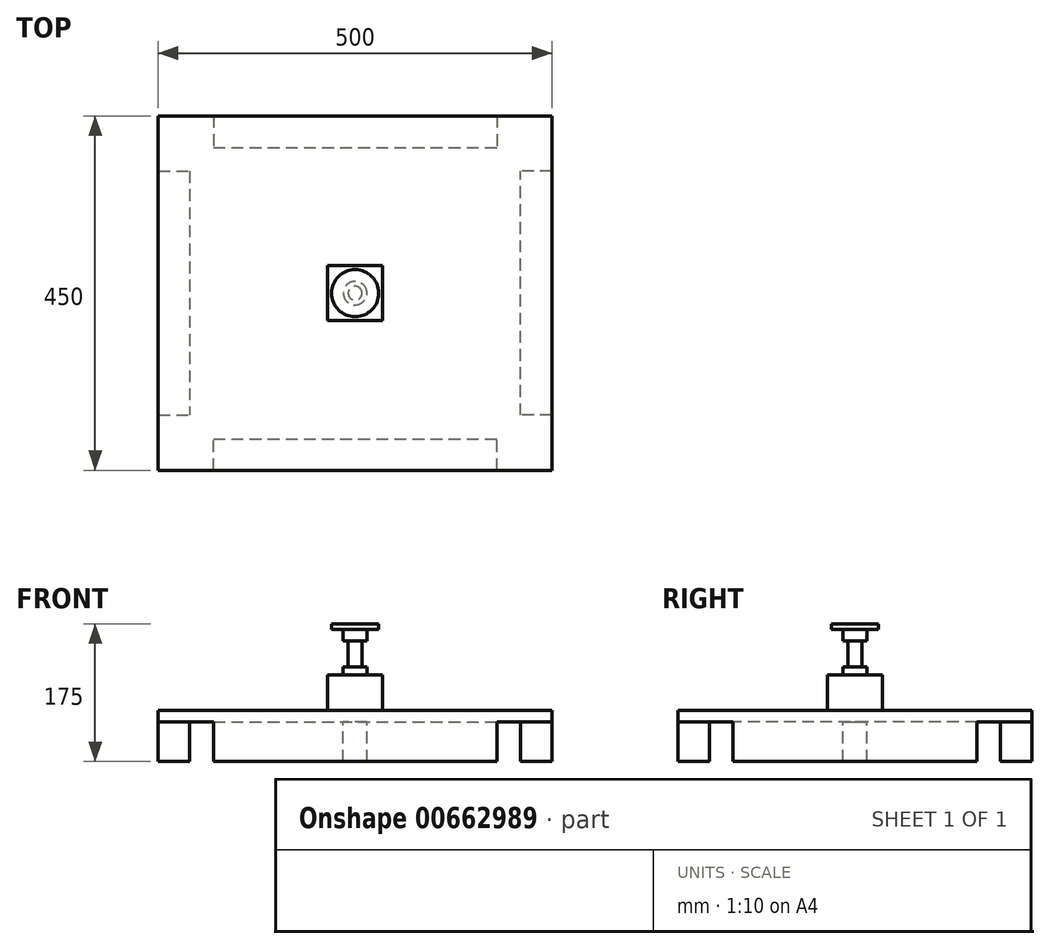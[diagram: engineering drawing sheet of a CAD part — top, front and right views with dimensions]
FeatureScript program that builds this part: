
annotation { "Feature Type Name" : "Feature", "Feature Type Description" : "" }
export const myFeature = defineFeature(function(context is Context, id is Id, definition is map)
    precondition{}
    {
        {
            var Q0;
            Q0=qCreatedBy(makeId("Top.planeOp"),FACE);
            var sketch = newSketch(context, id + "F0", { "sketchPlane" : qUnion([Q0])});
            skLineSegment(sketch, "E0.bottom", {"start": v(250, -225) * mm, "end": v(-250, -225) * mm});
            skLineSegment(sketch, "E0.top", {"start": v(250, 225) * mm, "end": v(-250, 225) * mm});
            skLineSegment(sketch, "E0.left", {"start": v(250, -225) * mm, "end": v(250, 225) * mm});
            skLineSegment(sketch, "E0.right", {"start": v(-250, -225) * mm, "end": v(-250, 225) * mm});
            skPoint(sketch, "E0.middle", {"position": v(0, 0) * mm});
            skLineSegment(sketch, "E1.bottom", {"start": v(-180, -225) * mm, "end": v(180, -225) * mm});
            skLineSegment(sketch, "E1.top", {"start": v(-180, -185) * mm, "end": v(180, -185) * mm});
            skLineSegment(sketch, "E1.left", {"start": v(-180, -225) * mm, "end": v(-180, -185) * mm});
            skLineSegment(sketch, "E1.right", {"start": v(180, -225) * mm, "end": v(180, -185) * mm});
            skLineSegment(sketch, "E2.bottom", {"start": v(250, -155) * mm, "end": v(210, -155) * mm});
            skLineSegment(sketch, "E2.top", {"start": v(250, 155) * mm, "end": v(210, 155) * mm});
            skLineSegment(sketch, "E2.left", {"start": v(250, -155) * mm, "end": v(250, 155) * mm});
            skLineSegment(sketch, "E2.right", {"start": v(210, -155) * mm, "end": v(210, 155) * mm});
            skLineSegment(sketch, "E3.bottom", {"start": v(-180, 225) * mm, "end": v(180, 225) * mm});
            skLineSegment(sketch, "E3.top", {"start": v(-180, 185) * mm, "end": v(180, 185) * mm});
            skLineSegment(sketch, "E3.left", {"start": v(-180, 225) * mm, "end": v(-180, 185) * mm});
            skLineSegment(sketch, "E3.right", {"start": v(180, 225) * mm, "end": v(180, 185) * mm});
            skLineSegment(sketch, "E4.bottom", {"start": v(-250, 155) * mm, "end": v(-210, 155) * mm});
            skLineSegment(sketch, "E4.top", {"start": v(-250, -155) * mm, "end": v(-210, -155) * mm});
            skLineSegment(sketch, "E4.left", {"start": v(-250, 155) * mm, "end": v(-250, -155) * mm});
            skLineSegment(sketch, "E4.right", {"start": v(-210, 155) * mm, "end": v(-210, -155) * mm});
            skLineSegment(sketch, "E5", {"start": v(180, 185) * mm, "end": v(210, 185) * mm, "construction": true});
            skLineSegment(sketch, "E6", {"start": v(210, 185) * mm, "end": v(210, 155) * mm, "construction": true});
            skLineSegment(sketch, "E7", {"start": v(210, -155) * mm, "end": v(210, -185) * mm, "construction": true});
            skLineSegment(sketch, "E8", {"start": v(210, -185) * mm, "end": v(180, -185) * mm, "construction": true});
            skLineSegment(sketch, "E9", {"start": v(-180, -185) * mm, "end": v(-210, -185) * mm, "construction": true});
            skLineSegment(sketch, "E10", {"start": v(-210, -185) * mm, "end": v(-210, -155) * mm, "construction": true});
            skLineSegment(sketch, "E11", {"start": v(-210, 155) * mm, "end": v(-210, 185) * mm, "construction": true});
            skLineSegment(sketch, "E12", {"start": v(-210, 185) * mm, "end": v(-180, 185) * mm, "construction": true});
            skSolve(sketch);
        }
        {
            var Q0;
            Q0=makeQuery(id+"F0.imprint","IMPRINT",FACE,{"disambiguationData":[TD([[makeQuery(id+"F0.imprint","IMPRINT",EDGE,{"derivedFrom":sQuery(id+"F0.wireOp",EDGE,"E1.top")}),1.0]])]});
            var Q1;
            {var subQ2=sQuery(id+"F0.wireOp",EDGE,"E4.bottom");Q1=makeQuery(id+"F0.imprint","IMPRINT",FACE,{"disambiguationData":[TD([[makeQuery(id+"F0.imprint","IMPRINT",EDGE,{"derivedFrom":subQ2}),-1.0]])]});}
            var Q2;
            Q2=makeQuery(id+"F0.imprint","IMPRINT",FACE,{"disambiguationData":[TD([[makeQuery(id+"F0.imprint","IMPRINT",EDGE,{"derivedFrom":sQuery(id+"F0.wireOp",EDGE,"E3.top")}),1.0]])]});
            var Q3;
            {var subQ0=sQuery(id+"F0.wireOp",EDGE,"E2.bottom");Q3=makeQuery(id+"F0.imprint","IMPRINT",FACE,{"disambiguationData":[TD([[makeQuery(id+"F0.imprint","IMPRINT",EDGE,{"derivedFrom":subQ0}),-1.0]])]});}
            var Q4;
            Q4=makeQuery(id+"F0.imprint","IMPRINT",FACE,{"disambiguationData":[TD([[makeQuery(id+"F0.imprint","IMPRINT",EDGE,{"derivedFrom":sQuery(id+"F0.wireOp",EDGE,"E1.top")}),-1.0]])]});
            extrude(context, id + "F1", {"entities" : qUnion([Q0, Q1, Q2, Q3, Q4]), "depth" : 15 * mm, "offsetDistance" : 25 * mm});
        }
        {
            var Q0;
            Q0=makeQuery(id+"F0.imprint","IMPRINT",FACE,{"disambiguationData":[TD([[makeQuery(id+"F0.imprint","IMPRINT",EDGE,{"derivedFrom":sQuery(id+"F0.wireOp",EDGE,"E1.top")}),-1.0]])]});
            var Q1;
            {var subQ2=sQuery(id+"F0.wireOp",EDGE,"E4.bottom");Q1=makeQuery(id+"F0.imprint","IMPRINT",FACE,{"disambiguationData":[TD([[makeQuery(id+"F0.imprint","IMPRINT",EDGE,{"derivedFrom":subQ2}),-1.0]])]});}
            var Q2;
            Q2=makeQuery(id+"F0.imprint","IMPRINT",FACE,{"disambiguationData":[TD([[makeQuery(id+"F0.imprint","IMPRINT",EDGE,{"derivedFrom":sQuery(id+"F0.wireOp",EDGE,"E3.top")}),1.0]])]});
            var Q3;
            {var subQ0=sQuery(id+"F0.wireOp",EDGE,"E2.bottom");Q3=makeQuery(id+"F0.imprint","IMPRINT",FACE,{"disambiguationData":[TD([[makeQuery(id+"F0.imprint","IMPRINT",EDGE,{"derivedFrom":subQ0}),-1.0]])]});}
            extrude(context, id + "F2", {"entities" : qUnion([Q0, Q1, Q2, Q3]), "operationType" : NewBodyOperationType.ADD, "oppositeDirection" : true, "depth" : 50 * mm, "offsetDistance" : 25 * mm});
        }
        {
            var Q0;
            Q0=sQuery(id+"F0.wireOp",VERTEX,"E0.middle");
            var Q1;
            Q1=makeQuery(id+"F1.opExtrude","SWEPT_BODY",BODY,{"disambiguationData":[OSD([sQuery(id+"F0.wireOp",EDGE,"E0.bottom"),sQuery(id+"F0.wireOp",EDGE,"E0.top"),sQuery(id+"F0.wireOp",EDGE,"E0.left"),sQuery(id+"F0.wireOp",EDGE,"E0.right")])]});
            hole(context, id + "F3", {"style" : HoleStyle.SIMPLE, "endStyle" : HoleEndStyle.THROUGH, "oppositeDirection" : true, "standardTappedOrClearance" : lookupTablePath({ "standard" : "ISO", "engagement" : "75%", "pitch" : "1.5 mm", "size" : "M10", "type" : "Tapped" }), "standardBlindInLast" : lookupTablePath({ "fit" : "Normal", "standard" : "ISO", "engagement" : "75%", "pitch" : "1.5 mm", "size" : "M10", "type" : "Clearance & tapped" }), "holeDiameter" : 8.5 * mm, "majorDiameter" : 10 * mm, "showTappedDepth" : true, "isTappedThrough" : true, "tappedDepth" : 12 * mm, "tapClearance" : 3, "locations" : qUnion([Q0]), "scope" : qUnion([Q1])});
        }
        {
            var Q0;
            Q0=qCreatedBy(makeId("Top.planeOp"),FACE);
            var sketch = newSketch(context, id + "F4", { "sketchPlane" : qUnion([Q0])});
            skLineSegment(sketch, "E13.bottom", {"start": v(35, -35) * mm, "end": v(-35, -35) * mm});
            skLineSegment(sketch, "E13.top", {"start": v(35, 35) * mm, "end": v(-35, 35) * mm});
            skLineSegment(sketch, "E13.left", {"start": v(35, -35) * mm, "end": v(35, 35) * mm});
            skLineSegment(sketch, "E13.right", {"start": v(-35, -35) * mm, "end": v(-35, 35) * mm});
            skPoint(sketch, "E13.middle", {"position": v(0, 0) * mm});
            skSolve(sketch);
        }
        {
            var Q0;
            Q0=makeQuery(id+"F4.imprint","IMPRINT",FACE,{"disambiguationData":[TD([[makeQuery(id+"F4.imprint","IMPRINT",EDGE,{"derivedFrom":sQuery(id+"F4.wireOp",EDGE,"E13.bottom")}),-1.0]])]});
            extrude(context, id + "F5", {"entities" : qUnion([Q0]), "depth" : 60 * mm, "offsetDistance" : 25 * mm});
        }
        {
            var Q0;
            Q0=makeQuery(id+"F5.opExtrude","CAP_FACE",FACE,{"disambiguationData":[OSD([sQuery(id+"F4.wireOp",EDGE,"E13.bottom"),sQuery(id+"F4.wireOp",EDGE,"E13.top"),sQuery(id+"F4.wireOp",EDGE,"E13.left"),sQuery(id+"F4.wireOp",EDGE,"E13.right")])],"isStart":false});
            var sketch = newSketch(context, id + "F6", { "sketchPlane" : qUnion([Q0])});
            skCircle(sketch, "E14", {"center": v(0, 0) * mm, "radius": 15 * mm});
            skSolve(sketch);
        }
        {
            var Q0;
            Q0=makeQuery(id+"F6.imprint","IMPRINT",FACE,{"disambiguationData":[TD([[makeQuery(id+"F6.imprint","IMPRINT",EDGE,{"derivedFrom":sQuery(id+"F6.wireOp",EDGE,"E14")}),1.0]])]});
            extrude(context, id + "F7", {"entities" : qUnion([Q0]), "operationType" : NewBodyOperationType.ADD, "depth" : 10 * mm, "offsetDistance" : 25 * mm});
        }
        {
            var Q0;
            Q0=makeQuery(id+"F7.opExtrude","CAP_FACE",FACE,{"disambiguationData":[OSD([sQuery(id+"F6.wireOp",EDGE,"E14")])],"isStart":false});
            var sketch = newSketch(context, id + "F8", { "sketchPlane" : qUnion([Q0])});
            skCircle(sketch, "E15", {"center": v(0, 0) * mm, "radius": 8.75 * mm});
            skSolve(sketch);
        }
        {
            var Q0;
            Q0=makeQuery(id+"F8.imprint","IMPRINT",FACE,{"disambiguationData":[TD([[makeQuery(id+"F8.imprint","IMPRINT",EDGE,{"derivedFrom":sQuery(id+"F8.wireOp",EDGE,"E15")}),1.0]])]});
            extrude(context, id + "F9", {"entities" : qUnion([Q0]), "operationType" : NewBodyOperationType.ADD, "depth" : 33 * mm, "offsetDistance" : 25 * mm});
        }
        {
            var Q0;
            Q0=makeQuery(id+"F9.opExtrude","CAP_FACE",FACE,{"disambiguationData":[OSD([sQuery(id+"F8.wireOp",EDGE,"E15")])],"isStart":false});
            var sketch = newSketch(context, id + "F10", { "sketchPlane" : qUnion([Q0])});
            skCircle(sketch, "E16", {"center": v(0, 0) * mm, "radius": 15 * mm});
            skSolve(sketch);
        }
        {
            var Q0;
            Q0=makeQuery(id+"F10.imprint","IMPRINT",FACE,{"disambiguationData":[TD([[makeQuery(id+"F10.imprint","IMPRINT",EDGE,{"derivedFrom":sQuery(id+"F10.wireOp",EDGE,"E16")}),1.0]])]});
            var Q1;
            Q1=makeQuery(id+"F10.imprint","IMPRINT",FACE,{"disambiguationData":[TD([[makeQuery(id+"F10.imprint","IMPRINT",EDGE,{"derivedFrom":makeQuery(id+"F9.opExtrude","CAP_EDGE",EDGE,{"disambiguationData":[OSD([sQuery(id+"F8.wireOp",EDGE,"E15")])],"isStart":false})}),1.0]])]});
            extrude(context, id + "F11", {"entities" : qUnion([Q0, Q1]), "operationType" : NewBodyOperationType.ADD, "depth" : 15 * mm, "offsetDistance" : 25 * mm});
        }
        {
            var Q0;
            Q0=makeQuery(id+"F11.opExtrude","CAP_FACE",FACE,{"disambiguationData":[OSD([sQuery(id+"F10.wireOp",EDGE,"E16")])],"isStart":false});
            var sketch = newSketch(context, id + "F12", { "sketchPlane" : qUnion([Q0])});
            skCircle(sketch, "E17", {"center": v(0, 0) * mm, "radius": 30 * mm});
            skSolve(sketch);
        }
        {
            var Q0;
            Q0=makeQuery(id+"F12.imprint","IMPRINT",FACE,{"disambiguationData":[TD([[makeQuery(id+"F12.imprint","IMPRINT",EDGE,{"derivedFrom":sQuery(id+"F12.wireOp",EDGE,"E17")}),1.0]])]});
            var Q1;
            Q1=makeQuery(id+"F12.imprint","IMPRINT",FACE,{"disambiguationData":[TD([[makeQuery(id+"F12.imprint","IMPRINT",EDGE,{"derivedFrom":makeQuery(id+"F11.opExtrude","CAP_EDGE",EDGE,{"disambiguationData":[OSD([sQuery(id+"F10.wireOp",EDGE,"E16")])],"isStart":false})}),1.0]])]});
            extrude(context, id + "F13", {"entities" : qUnion([Q0, Q1]), "operationType" : NewBodyOperationType.ADD, "depth" : 7 * mm, "offsetDistance" : 25 * mm});
        }
        {
            var Q0;
            Q0=makeQuery(id+"F5.opExtrude","CAP_FACE",FACE,{"disambiguationData":[OSD([sQuery(id+"F4.wireOp",EDGE,"E13.bottom"),sQuery(id+"F4.wireOp",EDGE,"E13.top"),sQuery(id+"F4.wireOp",EDGE,"E13.left"),sQuery(id+"F4.wireOp",EDGE,"E13.right")])],"isStart":true});
            var sketch = newSketch(context, id + "F14", { "sketchPlane" : qUnion([Q0])});
            skCircle(sketch, "E18", {"center": v(0, 0) * mm, "radius": 15 * mm});
            skSolve(sketch);
        }
        {
            var Q0;
            Q0=makeQuery(id+"F14.imprint","IMPRINT",FACE,{"disambiguationData":[TD([[makeQuery(id+"F14.imprint","IMPRINT",EDGE,{"derivedFrom":sQuery(id+"F14.wireOp",EDGE,"E18")}),1.0]])]});
            extrude(context, id + "F15", {"entities" : qUnion([Q0]), "operationType" : NewBodyOperationType.ADD, "depth" : 50 * mm, "offsetDistance" : 25 * mm});
        }
    });
